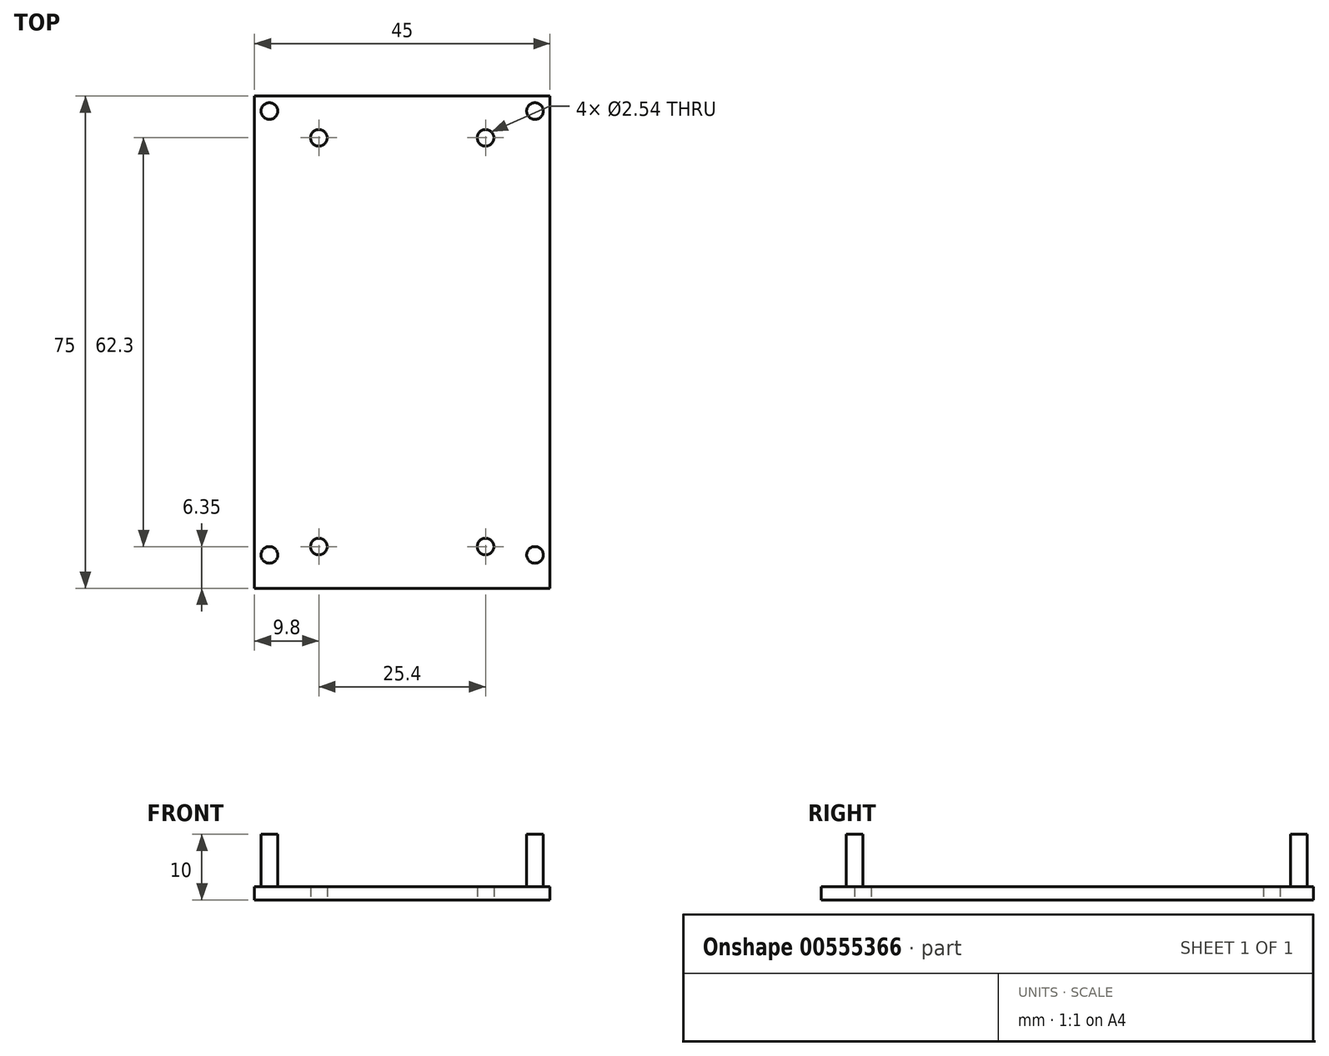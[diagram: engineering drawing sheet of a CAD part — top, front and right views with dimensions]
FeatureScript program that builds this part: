
annotation { "Feature Type Name" : "Feature", "Feature Type Description" : "" }
export const myFeature = defineFeature(function(context is Context, id is Id, definition is map)
    precondition{}
    {
        {
            var Q0;
            Q0=qCreatedBy(makeId("Top.planeOp"),FACE);
            var sketch = newSketch(context, id + "F0", { "sketchPlane" : qUnion([Q0])});
            skLineSegment(sketch, "E0.bottom", {"start": v(22.5, -37.5) * mm, "end": v(-22.5, -37.5) * mm});
            skLineSegment(sketch, "E0.top", {"start": v(22.5, 37.5) * mm, "end": v(-22.5, 37.5) * mm});
            skLineSegment(sketch, "E0.left", {"start": v(22.5, -37.5) * mm, "end": v(22.5, 37.5) * mm});
            skLineSegment(sketch, "E0.right", {"start": v(-22.5, -37.5) * mm, "end": v(-22.5, 37.5) * mm});
            skPoint(sketch, "E0.middle", {"position": v(0, 0) * mm});
            skLineSegment(sketch, "E1.0", {"start": v(-21.5, -36.5) * mm, "end": v(-21.5, 36.5) * mm, "construction": true});
            skLineSegment(sketch, "E1.2", {"start": v(21.5, -36.5) * mm, "end": v(21.5, 36.5) * mm, "construction": true});
            skLineSegment(sketch, "E1.3", {"start": v(21.5, 36.5) * mm, "end": v(-21.5, 36.5) * mm, "construction": true});
            skCircle(sketch, "E2", {"center": v(-20.23, -32.42) * mm, "radius": 1.27 * mm});
            skCircle(sketch, "E3", {"center": v(20.23, -32.42) * mm, "radius": 1.27 * mm});
            skCircle(sketch, "E4", {"center": v(20.23, 35.23) * mm, "radius": 1.27 * mm});
            skCircle(sketch, "E5", {"center": v(-20.23, 35.23) * mm, "radius": 1.27 * mm});
            skLineSegment(sketch, "E6", {"start": v(-22.5, -31.15) * mm, "end": v(22.5, -31.15) * mm, "construction": true});
            skLineSegment(sketch, "E7", {"start": v(-22.5, 31.15) * mm, "end": v(22.5, 31.15) * mm, "construction": true});
            skCircle(sketch, "E8", {"center": v(-12.7, -31.15) * mm, "radius": 1.27 * mm});
            skCircle(sketch, "E9", {"center": v(12.7, -31.15) * mm, "radius": 1.27 * mm});
            skCircle(sketch, "E10", {"center": v(-12.7, 31.15) * mm, "radius": 1.27 * mm});
            skCircle(sketch, "E11", {"center": v(12.7, 31.15) * mm, "radius": 1.27 * mm});
            skLineSegment(sketch, "E12", {"start": v(-21.5, -36.5) * mm, "end": v(21.5, -36.5) * mm, "construction": true});
            skSolve(sketch);
        }
        {
            var Q0;
            Q0=makeQuery(id+"F0.imprint","IMPRINT",FACE,{"disambiguationData":[TD([[makeQuery(id+"F0.imprint","IMPRINT",EDGE,{"derivedFrom":sQuery(id+"F0.wireOp",EDGE,"E0.bottom")}),-1.0]])]});
            var Q1;
            Q1=makeQuery(id+"F0.imprint","IMPRINT",FACE,{"disambiguationData":[TD([[makeQuery(id+"F0.imprint","IMPRINT",EDGE,{"derivedFrom":sQuery(id+"F0.wireOp",EDGE,"E1.0")}),-1.0]])]});
            var Q2;
            Q2=makeQuery(id+"F0.imprint","IMPRINT",FACE,{"disambiguationData":[TD([[makeQuery(id+"F0.imprint","IMPRINT",EDGE,{"derivedFrom":sQuery(id+"F0.wireOp",EDGE,"E2")}),1.0]])]});
            var Q3;
            Q3=makeQuery(id+"F0.imprint","IMPRINT",FACE,{"disambiguationData":[TD([[makeQuery(id+"F0.imprint","IMPRINT",EDGE,{"derivedFrom":sQuery(id+"F0.wireOp",EDGE,"E3")}),1.0]])]});
            var Q4;
            Q4=makeQuery(id+"F0.imprint","IMPRINT",FACE,{"disambiguationData":[TD([[makeQuery(id+"F0.imprint","IMPRINT",EDGE,{"derivedFrom":sQuery(id+"F0.wireOp",EDGE,"E4")}),1.0]])]});
            var Q5;
            Q5=makeQuery(id+"F0.imprint","IMPRINT",FACE,{"disambiguationData":[TD([[makeQuery(id+"F0.imprint","IMPRINT",EDGE,{"derivedFrom":sQuery(id+"F0.wireOp",EDGE,"E5")}),1.0]])]});
            extrude(context, id + "F1", {"entities" : qUnion([Q0, Q1, Q2, Q3, Q4, Q5]), "depth" : 2 * mm, "offsetDistance" : 25.4 * mm});
        }
        {
            var Q0;
            Q0=makeQuery(id+"F0.imprint","IMPRINT",FACE,{"disambiguationData":[TD([[makeQuery(id+"F0.imprint","IMPRINT",EDGE,{"derivedFrom":sQuery(id+"F0.wireOp",EDGE,"E5")}),1.0]])]});
            var Q1;
            Q1=makeQuery(id+"F0.imprint","IMPRINT",FACE,{"disambiguationData":[TD([[makeQuery(id+"F0.imprint","IMPRINT",EDGE,{"derivedFrom":sQuery(id+"F0.wireOp",EDGE,"E3")}),1.0]])]});
            var Q2;
            Q2=makeQuery(id+"F0.imprint","IMPRINT",FACE,{"disambiguationData":[TD([[makeQuery(id+"F0.imprint","IMPRINT",EDGE,{"derivedFrom":sQuery(id+"F0.wireOp",EDGE,"E2")}),1.0]])]});
            var Q3;
            Q3=makeQuery(id+"F0.imprint","IMPRINT",FACE,{"disambiguationData":[TD([[makeQuery(id+"F0.imprint","IMPRINT",EDGE,{"derivedFrom":sQuery(id+"F0.wireOp",EDGE,"E4")}),1.0]])]});
            extrude(context, id + "F2", {"entities" : qUnion([Q0, Q1, Q2, Q3]), "operationType" : NewBodyOperationType.ADD, "depth" : 10 * mm, "offsetDistance" : 25.4 * mm});
        }
    });
